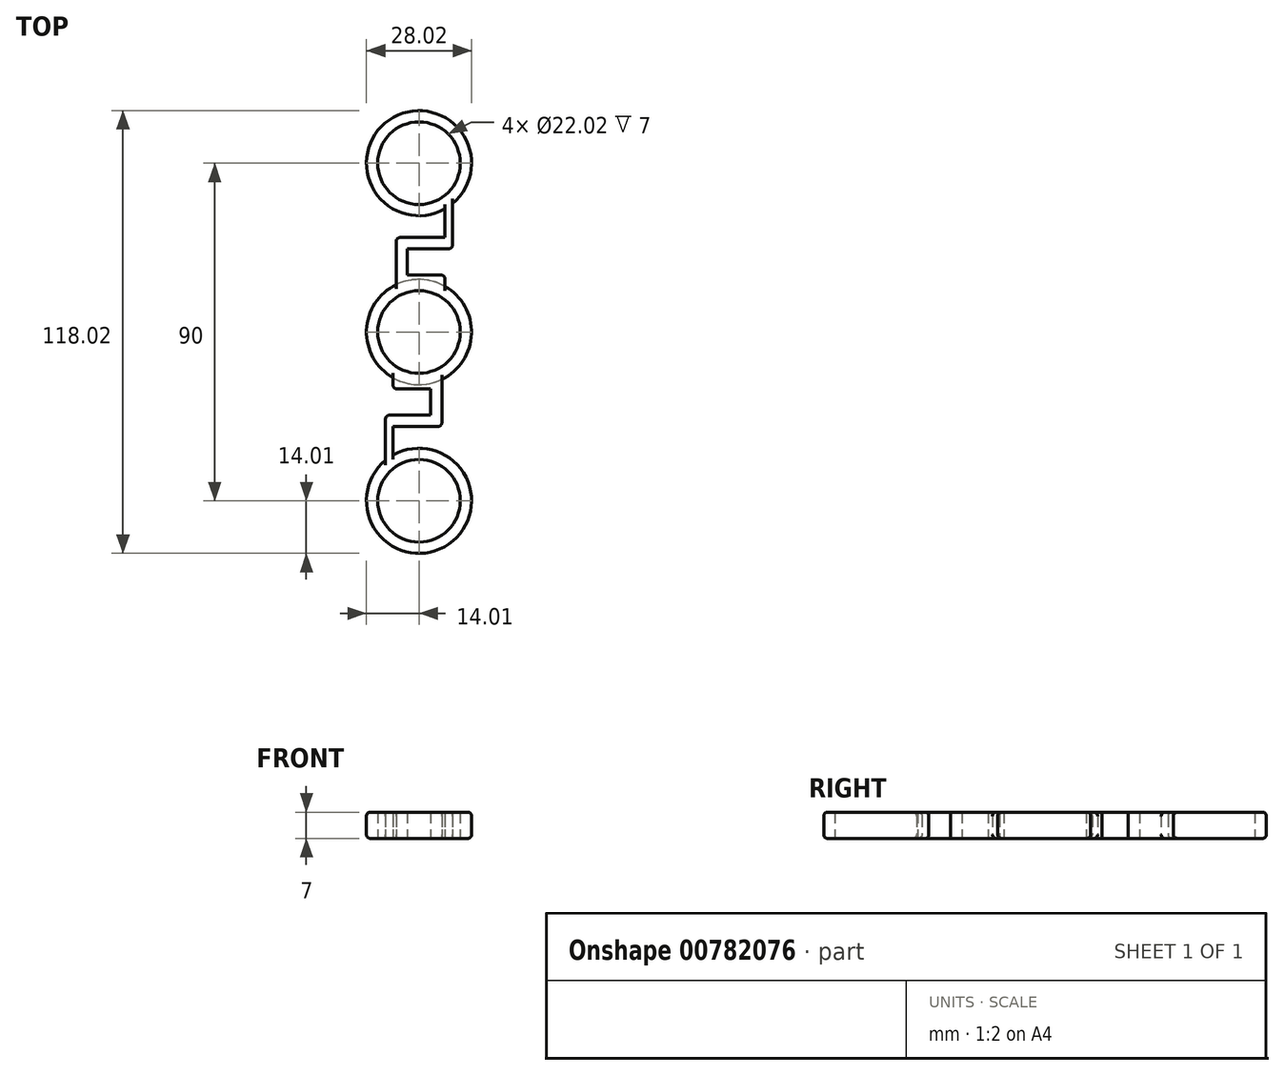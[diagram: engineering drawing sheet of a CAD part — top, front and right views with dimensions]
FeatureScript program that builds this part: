
annotation { "Feature Type Name" : "Feature", "Feature Type Description" : "" }
export const myFeature = defineFeature(function(context is Context, id is Id, definition is map)
    precondition{}
    {
        {
            var Q0;
            Q0=qCreatedBy(makeId("Top.planeOp"),FACE);
            var sketch = newSketch(context, id + "F0", { "sketchPlane" : qUnion([Q0])});
            skCircle(sketch, "E0", {"center": v(0, 0) * mm, "radius": 11.01 * mm});
            skCircle(sketch, "E1", {"center": v(0, 45) * mm, "radius": 11.01 * mm});
            skCircle(sketch, "E2.0", {"center": v(0, 45) * mm, "radius": 14.01 * mm});
            skCircle(sketch, "E3.0", {"center": v(0, 0) * mm, "radius": 14.01 * mm});
            skLineSegment(sketch, "E4.bottom", {"start": v(-11.01, 0) * mm, "end": v(11.01, 0) * mm});
            skLineSegment(sketch, "E4.top", {"start": v(-11.01, 45) * mm, "end": v(11.01, 45) * mm});
            skLineSegment(sketch, "E4.left", {"start": v(-11.01, 0) * mm, "end": v(-11.01, 45) * mm});
            skLineSegment(sketch, "E4.right", {"start": v(11.01, 0) * mm, "end": v(11.01, 45) * mm});
            skLineSegment(sketch, "E5.bottom", {"start": v(6.92, 12.18) * mm, "end": v(-6.08, 12.18) * mm});
            skLineSegment(sketch, "E5.top", {"start": v(6.92, 15.18) * mm, "end": v(-6.08, 15.18) * mm});
            skLineSegment(sketch, "E5.left", {"start": v(6.92, 12.18) * mm, "end": v(6.92, 15.18) * mm});
            skLineSegment(sketch, "E5.right", {"start": v(-6.08, 12.18) * mm, "end": v(-6.08, 15.18) * mm});
            skLineSegment(sketch, "E6.bottom", {"start": v(-6.08, 15.18) * mm, "end": v(-3.08, 15.18) * mm});
            skLineSegment(sketch, "E6.top", {"start": v(-6.08, 22.18) * mm, "end": v(-3.08, 22.18) * mm});
            skLineSegment(sketch, "E6.left", {"start": v(-6.08, 15.18) * mm, "end": v(-6.08, 22.18) * mm});
            skLineSegment(sketch, "E6.right", {"start": v(-3.08, 15.18) * mm, "end": v(-3.08, 22.18) * mm});
            skLineSegment(sketch, "E7.bottom", {"start": v(-6.08, 22.18) * mm, "end": v(8.92, 22.18) * mm});
            skLineSegment(sketch, "E7.top", {"start": v(-6.08, 25.18) * mm, "end": v(8.92, 25.18) * mm});
            skLineSegment(sketch, "E7.left", {"start": v(-6.08, 22.18) * mm, "end": v(-6.08, 25.18) * mm});
            skLineSegment(sketch, "E7.right", {"start": v(8.92, 22.18) * mm, "end": v(8.92, 25.18) * mm});
            skLineSegment(sketch, "E8.bottom", {"start": v(8.92, 25.18) * mm, "end": v(6.92, 25.18) * mm});
            skLineSegment(sketch, "E8.top", {"start": v(8.92, 32.82) * mm, "end": v(6.92, 32.82) * mm});
            skLineSegment(sketch, "E8.left", {"start": v(8.92, 25.18) * mm, "end": v(8.92, 32.82) * mm});
            skLineSegment(sketch, "E8.right", {"start": v(6.92, 25.18) * mm, "end": v(6.92, 32.82) * mm});
            skLineSegment(sketch, "E9.bottom", {"start": v(8.92, 32.82) * mm, "end": v(-6.08, 32.82) * mm});
            skLineSegment(sketch, "E9.top", {"start": v(8.92, 35.82) * mm, "end": v(-6.08, 35.82) * mm});
            skLineSegment(sketch, "E9.left", {"start": v(8.92, 32.82) * mm, "end": v(8.92, 35.82) * mm});
            skLineSegment(sketch, "E9.right", {"start": v(-6.08, 32.82) * mm, "end": v(-6.08, 35.82) * mm});
            skSolve(sketch);
        }
        {
            var Q0;
            {var subQ0=sQuery(id+"F0.wireOp",EDGE,"E4.left");var subQ6=sQuery(id+"F0.wireOp",EDGE,"E2.0");var subQ7=makeQuery(id+"F0.imprint","INTERSECT",VERTEX,{"derivedFrom":[subQ6,subQ0]});Q0=makeQuery(id+"F0.imprint","IMPRINT",FACE,{"disambiguationData":[TD([[makeQuery(id+"F0.imprint","IMPRINT",EDGE,{"disambiguationData":[TD([[subQ7,1.0]])],"derivedFrom":subQ6}),1.0]])]});}
            var Q1;
            {var subQ0=sQuery(id+"F0.wireOp",EDGE,"E9.bottom");Q1=makeQuery(id+"F0.imprint","IMPRINT",FACE,{"disambiguationData":[TD([[makeQuery(id+"F0.imprint","IMPRINT",EDGE,{"derivedFrom":subQ0}),1.0]])]});}
            var Q2;
            {var subQ3=sQuery(id+"F0.wireOp",EDGE,"E9.left");var subQ5=sQuery(id+"F0.wireOp",EDGE,"E2.0");var subQ6=makeQuery(id+"F0.imprint","INTERSECT",VERTEX,{"derivedFrom":[subQ5,subQ3]});Q2=makeQuery(id+"F0.imprint","IMPRINT",FACE,{"disambiguationData":[TD([[makeQuery(id+"F0.imprint","IMPRINT",EDGE,{"disambiguationData":[TD([[subQ6,-1.0]])],"derivedFrom":subQ5}),1.0]])]});}
            var Q3;
            {var subQ5=sQuery(id+"F0.wireOp",EDGE,"E9.bottom");Q3=makeQuery(id+"F0.imprint","IMPRINT",FACE,{"disambiguationData":[TD([[makeQuery(id+"F0.imprint","IMPRINT",EDGE,{"derivedFrom":subQ5}),-1.0]])]});}
            var Q4;
            Q4=makeQuery(id+"F0.imprint","IMPRINT",FACE,{"disambiguationData":[TD([[makeQuery(id+"F0.imprint","IMPRINT",EDGE,{"derivedFrom":sQuery(id+"F0.wireOp",EDGE,"E8.top")}),1.0]])]});
            var Q5;
            {var subQ0=sQuery(id+"F0.wireOp",EDGE,"E8.top");Q5=makeQuery(id+"F0.imprint","IMPRINT",FACE,{"disambiguationData":[TD([[makeQuery(id+"F0.imprint","IMPRINT",EDGE,{"derivedFrom":subQ0}),-1.0]])]});}
            var Q6;
            Q6=makeQuery(id+"F0.imprint","IMPRINT",FACE,{"disambiguationData":[TD([[makeQuery(id+"F0.imprint","IMPRINT",EDGE,{"derivedFrom":sQuery(id+"F0.wireOp",EDGE,"E6.top")}),1.0]])]});
            var Q7;
            Q7=makeQuery(id+"F0.imprint","IMPRINT",FACE,{"disambiguationData":[TD([[makeQuery(id+"F0.imprint","IMPRINT",EDGE,{"derivedFrom":sQuery(id+"F0.wireOp",EDGE,"E6.top")}),-1.0]])]});
            var Q8;
            {var subQ0=sQuery(id+"F0.wireOp",EDGE,"E5.left");Q8=makeQuery(id+"F0.imprint","IMPRINT",FACE,{"disambiguationData":[TD([[makeQuery(id+"F0.imprint","IMPRINT",EDGE,{"derivedFrom":subQ0}),1.0]])]});}
            var Q9;
            {var subQ0=sQuery(id+"F0.wireOp",EDGE,"E5.bottom");Q9=makeQuery(id+"F0.imprint","IMPRINT",FACE,{"disambiguationData":[TD([[makeQuery(id+"F0.imprint","IMPRINT",EDGE,{"derivedFrom":subQ0}),-1.0]])]});}
            var Q10;
            {var subQ10=sQuery(id+"F0.wireOp",EDGE,"E5.bottom");Q10=makeQuery(id+"F0.imprint","IMPRINT",FACE,{"disambiguationData":[TD([[makeQuery(id+"F0.imprint","IMPRINT",EDGE,{"derivedFrom":subQ10}),1.0]])]});}
            var Q11;
            {var subQ0=sQuery(id+"F0.wireOp",EDGE,"E4.left");var subQ6=sQuery(id+"F0.wireOp",EDGE,"E3.0");var subQ8=makeQuery(id+"F0.imprint","INTERSECT",VERTEX,{"derivedFrom":[subQ6,subQ0]});Q11=makeQuery(id+"F0.imprint","IMPRINT",FACE,{"disambiguationData":[TD([[makeQuery(id+"F0.imprint","IMPRINT",EDGE,{"disambiguationData":[TD([[subQ8,-1.0]])],"derivedFrom":subQ6}),1.0]])]});}
            extrude(context, id + "F1", {"entities" : qUnion([Q0, Q1, Q2, Q3, Q4, Q5, Q6, Q7, Q8, Q9, Q10, Q11]), "depth" : 7 * mm, "offsetDistance" : 25 * mm});
        }
        {
            var Q0;
            Q0=makeQuery(id+"F1.opExtrude","CAP_EDGE",EDGE,{"disambiguationData":[OSD([sQuery(id+"F0.wireOp",EDGE,"E3.0")])],"isStart":false});
            var Q1;
            Q1=makeQuery(id+"F1.opExtrude","CAP_EDGE",EDGE,{"disambiguationData":[OSD([sQuery(id+"F0.wireOp",EDGE,"E3.0")])],"isStart":true});
            var Q2;
            Q2=makeQuery(id+"F1.opExtrude","SWEPT_EDGE",EDGE,{"disambiguationData":[OSD([sQuery(id+"F0.wireOp",EDGE,"E7.top"),sQuery(id+"F0.wireOp",EDGE,"E7.left")])]});
            var Q3;
            Q3=makeQuery(id+"F1.opExtrude","SWEPT_EDGE",EDGE,{"disambiguationData":[OSD([sQuery(id+"F0.wireOp",EDGE,"E5.top"),sQuery(id+"F0.wireOp",EDGE,"E5.left")])]});
            var Q4;
            Q4=makeQuery(id+"F1.opExtrude","SWEPT_EDGE",EDGE,{"disambiguationData":[OSD([sQuery(id+"F0.wireOp",EDGE,"E7.bottom"),sQuery(id+"F0.wireOp",EDGE,"E7.right")])]});
            var Q5;
            Q5=makeQuery(id+"F1.opExtrude","CAP_EDGE",EDGE,{"disambiguationData":[OSD([sQuery(id+"F0.wireOp",EDGE,"E2.0")])],"isStart":false});
            var Q6;
            Q6=makeQuery(id+"F1.opExtrude","CAP_EDGE",EDGE,{"disambiguationData":[OSD([sQuery(id+"F0.wireOp",EDGE,"E2.0")])],"isStart":true});
            fillet(context, id + "F2", {"entities" : qUnion([Q0, Q1, Q2, Q3, Q4, Q5, Q6]), "radius" : 1 * mm, "tangentPropagation" : true, "allowEdgeOverflow" : false});
        }
        {
            var Q0;
            Q0=makeQuery(id+"F1.opExtrude","SWEPT_BODY",BODY,{"disambiguationData":[OSD([sQuery(id+"F0.wireOp",EDGE,"E0"),sQuery(id+"F0.wireOp",EDGE,"E1"),sQuery(id+"F0.wireOp",EDGE,"E2.0"),sQuery(id+"F0.wireOp",EDGE,"E3.0"),sQuery(id+"F0.wireOp",EDGE,"E5.top"),sQuery(id+"F0.wireOp",EDGE,"E5.left"),sQuery(id+"F0.wireOp",EDGE,"E5.right"),sQuery(id+"F0.wireOp",EDGE,"E6.left"),sQuery(id+"F0.wireOp",EDGE,"E6.right"),sQuery(id+"F0.wireOp",EDGE,"E7.bottom"),sQuery(id+"F0.wireOp",EDGE,"E7.top"),sQuery(id+"F0.wireOp",EDGE,"E7.left"),sQuery(id+"F0.wireOp",EDGE,"E7.right"),sQuery(id+"F0.wireOp",EDGE,"E8.left"),sQuery(id+"F0.wireOp",EDGE,"E8.right"),sQuery(id+"F0.wireOp",EDGE,"E9.left")])]});
            var Q1;
            Q1=makeQuery(id+"F1.opExtrude","SWEPT_FACE",FACE,{"disambiguationData":[OSD([sQuery(id+"F0.wireOp",EDGE,"E3.0")])]});
            circularPattern(context, id + "F3", {"entities" : qUnion([Q0]), "axis" : qUnion([Q1]), "angle" : 360 * degree, "instanceCount" : 2, "equalSpace" : true});
        }
    });
